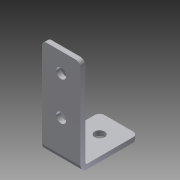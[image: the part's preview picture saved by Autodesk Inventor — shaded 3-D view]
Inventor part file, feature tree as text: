
AUTODESK INVENTOR PART (.ipt)
format: ipt  version: 2014 SP1 (Build 180222100, 222)  size: 184,320 bytes
history: native  units: in
note: dims shown in document units (in); Inventor stores cm internally (conversion verified against a paired STEP export)
features: other x4, sheet_metal_op x3, sketch x3, chamfer x1
ambient origin geometry x8: Origin, YZ Plane, XZ Plane, XY Plane, X Axis, Y Axis, Z Axis, Center Point
bodies: Solid1 (feature_tree)
feature tree (11):
  sheet_metal_op  "Face1"
  sheet_metal_op  "Flange1"
  chamfer  "Corner Round1"
  sketch  "Sketch1"  dims[d0=0.26in]
  other  "Plate1"
  sketch  "Sketch2"  dims[d2=1.0in]
  other  "Plate2"
  sheet_metal_op  "Bend1"
  sketch  "Sketch3"  dims[d3=1.5in d4=0.625in d5=0.375in d6=0.125in d7=0.125in d8=0.0625in d9=0.25in d10=0.125in d11=2.5in d12=90.0deg d13=0.05in d14=0.5in d15=0.125in d16=0.125in d17=1.0in d18=1.0in d19=0.26in d20=0.125in d21=0.0in d22=0.125in]
  other  "Cut1"
  other  "Definition1"
